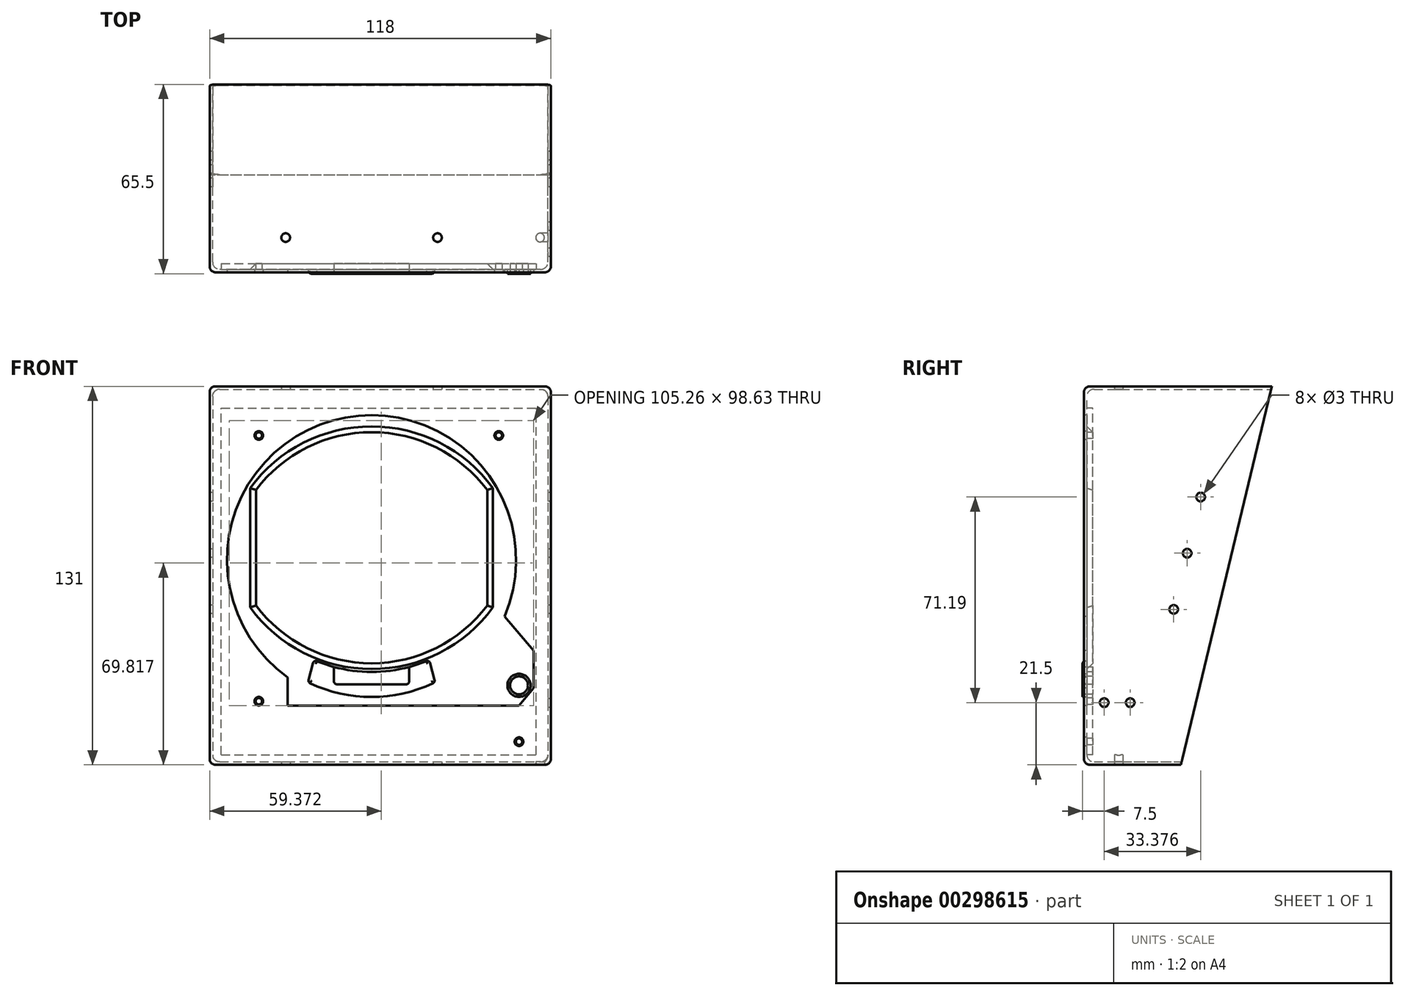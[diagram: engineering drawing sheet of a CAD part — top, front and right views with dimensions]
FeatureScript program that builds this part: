
annotation { "Feature Type Name" : "Feature", "Feature Type Description" : "" }
export const myFeature = defineFeature(function(context is Context, id is Id, definition is map)
    precondition{}
    {
        {
            var Q0;
            Q0=qCreatedBy(makeId("Front.planeOp"),FACE);
            var sketch = newSketch(context, id + "F0", { "sketchPlane" : qUnion([Q0])});
            skLineSegment(sketch, "E0.bottom", {"start": v(-52.84, -65.5) * mm, "end": v(-170.84, -65.5) * mm});
            skLineSegment(sketch, "E0.top", {"start": v(-52.84, 65.5) * mm, "end": v(-170.84, 65.5) * mm});
            skLineSegment(sketch, "E0.left", {"start": v(-52.84, -65.5) * mm, "end": v(-52.84, 65.5) * mm});
            skLineSegment(sketch, "E0.right", {"start": v(-170.84, -65.5) * mm, "end": v(-170.84, 65.5) * mm});
            skPoint(sketch, "E0.middle", {"position": v(-111.84, 0) * mm});
            skSolve(sketch);
        }
        {
            var Q0;
            Q0=makeQuery(id+"F0.imprint","IMPRINT",FACE,{"disambiguationData":[TD([[makeQuery(id+"F0.imprint","IMPRINT",EDGE,{"derivedFrom":sQuery(id+"F0.wireOp",EDGE,"E0.bottom")}),-1.0]])]});
            extrude(context, id + "F1", {"entities" : qUnion([Q0]), "endBound" : BoundingType.SYMMETRIC, "depth" : 120 * mm});
        }
        {
            var Q0;
            Q0=makeQuery(id+"F1.opExtrude","CAP_FACE",FACE,{"disambiguationData":[OSD([sQuery(id+"F0.wireOp",EDGE,"E0.bottom"),sQuery(id+"F0.wireOp",EDGE,"E0.top"),sQuery(id+"F0.wireOp",EDGE,"E0.left"),sQuery(id+"F0.wireOp",EDGE,"E0.right")])],"isStart":true});
            shell(context, id + "F2", {"entities" : qUnion([Q0]), "thickness" : 1 * mm});
        }
        {
            var Q0;
            Q0=makeQuery(id+"F1.opExtrude","SWEPT_FACE",FACE,{"disambiguationData":[OSD([sQuery(id+"F0.wireOp",EDGE,"E0.right")])]});
            var sketch = newSketch(context, id + "F3", { "sketchPlane" : qUnion([Q0])});
            skLineSegment(sketch, "E1", {"start": v(-5, 65.5) * mm, "end": v(26.45, -65.5) * mm});
            skLineSegment(sketch, "E2", {"start": v(26.45, -65.5) * mm, "end": v(-89.83, -65.5) * mm});
            skLineSegment(sketch, "E3", {"start": v(-89.83, -65.5) * mm, "end": v(-89.83, 65.5) * mm});
            skLineSegment(sketch, "E4", {"start": v(-89.83, 65.5) * mm, "end": v(-5, 65.5) * mm});
            skCircle(sketch, "E5", {"center": v(19.62, 27.19) * mm, "radius": 1.5 * mm});
            skCircle(sketch, "E6", {"center": v(28.96, -11.7) * mm, "radius": 1.5 * mm});
            skLineSegment(sketch, "E7", {"start": v(9.7, 4.24) * mm, "end": v(48.51, 13.56) * mm, "construction": true});
            skLineSegment(sketch, "E8", {"start": v(4.8, 24.66) * mm, "end": v(14.6, -16.18) * mm, "construction": true});
            skLineSegment(sketch, "E9", {"start": v(14.6, -16.18) * mm, "end": v(16.55, -15.71) * mm, "construction": true});
            skLineSegment(sketch, "E10", {"start": v(16.55, -15.71) * mm, "end": v(6.75, 25.13) * mm, "construction": true});
            skLineSegment(sketch, "E11", {"start": v(6.75, 25.13) * mm, "end": v(4.8, 24.66) * mm, "construction": true});
            skCircle(sketch, "E12", {"center": v(24.3, 7.74) * mm, "radius": 1.5 * mm});
            skSolve(sketch);
        }
        {
            var Q0;
            Q0=qSketchRegion(id+"F3",true);
            extrude(context, id + "F4", {"entities" : qUnion([Q0]), "operationType" : NewBodyOperationType.REMOVE, "oppositeDirection" : true, "depth" : 150 * mm});
        }
        {
            var Q0;
            Q0=makeQuery(id+"F1.opExtrude","CAP_EDGE",EDGE,{"disambiguationData":[OSD([sQuery(id+"F0.wireOp",EDGE,"E0.right")])],"isStart":false});
            var Q1;
            Q1=makeQuery(id+"F1.opExtrude","SWEPT_EDGE",EDGE,{"disambiguationData":[OSD([sQuery(id+"F0.wireOp",EDGE,"E0.top"),sQuery(id+"F0.wireOp",EDGE,"E0.right")])]});
            var Q2;
            Q2=makeQuery(id+"F1.opExtrude","CAP_EDGE",EDGE,{"disambiguationData":[OSD([sQuery(id+"F0.wireOp",EDGE,"E0.top")])],"isStart":false});
            var Q3;
            Q3=makeQuery(id+"F1.opExtrude","CAP_EDGE",EDGE,{"disambiguationData":[OSD([sQuery(id+"F0.wireOp",EDGE,"E0.left")])],"isStart":false});
            var Q4;
            Q4=makeQuery(id+"F1.opExtrude","SWEPT_EDGE",EDGE,{"disambiguationData":[OSD([sQuery(id+"F0.wireOp",EDGE,"E0.top"),sQuery(id+"F0.wireOp",EDGE,"E0.left")])]});
            var Q5;
            Q5=makeQuery(id+"F1.opExtrude","CAP_EDGE",EDGE,{"disambiguationData":[OSD([sQuery(id+"F0.wireOp",EDGE,"E0.bottom")])],"isStart":false});
            var Q6;
            Q6=makeQuery(id+"F1.opExtrude","SWEPT_EDGE",EDGE,{"disambiguationData":[OSD([sQuery(id+"F0.wireOp",EDGE,"E0.bottom"),sQuery(id+"F0.wireOp",EDGE,"E0.left")])]});
            var Q7;
            Q7=makeQuery(id+"F1.opExtrude","SWEPT_EDGE",EDGE,{"disambiguationData":[OSD([sQuery(id+"F0.wireOp",EDGE,"E0.bottom"),sQuery(id+"F0.wireOp",EDGE,"E0.right")])]});
            fillet(context, id + "F5", {"entities" : qUnion([Q0, Q1, Q2, Q3, Q4, Q5, Q6, Q7]), "radius" : 2 * mm, "tangentPropagation" : true, "allowEdgeOverflow" : false});
        }
        {
            var Q0;
            Q0=makeQuery(id+"F1.opExtrude","CAP_FACE",FACE,{"disambiguationData":[OSD([sQuery(id+"F0.wireOp",EDGE,"E0.bottom"),sQuery(id+"F0.wireOp",EDGE,"E0.top"),sQuery(id+"F0.wireOp",EDGE,"E0.left"),sQuery(id+"F0.wireOp",EDGE,"E0.right")])],"isStart":false});
            var sketch = newSketch(context, id + "F6", { "sketchPlane" : qUnion([Q0])});
            skCircle(sketch, "E13", {"center": v(-114.84, 5.5) * mm, "radius": 50 * mm});
            skLineSegment(sketch, "E14", {"start": v(-143.84, -35.23) * mm, "end": v(-143.84, -45) * mm});
            skLineSegment(sketch, "E15", {"start": v(-143.84, -45) * mm, "end": v(-63.84, -45) * mm});
            skLineSegment(sketch, "E16", {"start": v(-63.84, -45) * mm, "end": v(-58.84, -39) * mm});
            skLineSegment(sketch, "E17", {"start": v(-58.84, -39) * mm, "end": v(-58.84, -26) * mm});
            skLineSegment(sketch, "E18", {"start": v(-58.84, -26) * mm, "end": v(-68.86, -14.15) * mm});
            skCircle(sketch, "E19", {"center": v(-153.84, 48.5) * mm, "radius": 1.5 * mm});
            skCircle(sketch, "E20", {"center": v(-70.84, 48.5) * mm, "radius": 1.5 * mm});
            skCircle(sketch, "E21", {"center": v(-153.84, -43.5) * mm, "radius": 1.5 * mm});
            skCircle(sketch, "E22", {"center": v(-63.84, -57.5) * mm, "radius": 1.5 * mm});
            skSolve(sketch);
        }
        {
            var Q0;
            Q0=qSketchRegion(id+"F6",true);
            extrude(context, id + "F7", {"entities" : qUnion([Q0]), "operationType" : NewBodyOperationType.REMOVE, "oppositeDirection" : true, "depth" : 1 * mm});
        }
        {
            var Q0;
            Q0=makeQuery(id+"F2.opShell","OFFSET_FACE",FACE,{"disambiguationData":[OSD([sQuery(id+"F0.wireOp",EDGE,"E0.bottom"),sQuery(id+"F0.wireOp",EDGE,"E0.top"),sQuery(id+"F0.wireOp",EDGE,"E0.left"),sQuery(id+"F0.wireOp",EDGE,"E0.right")])]});
            var sketch = newSketch(context, id + "F8", { "sketchPlane" : qUnion([Q0])});
            skLineSegment(sketch, "E23.bottom", {"start": v(166.84, -62) * mm, "end": v(57.84, -62) * mm});
            skLineSegment(sketch, "E23.top", {"start": v(166.84, 58) * mm, "end": v(57.84, 58) * mm});
            skLineSegment(sketch, "E23.left", {"start": v(166.84, -62) * mm, "end": v(166.84, 58) * mm});
            skLineSegment(sketch, "E23.right", {"start": v(57.84, -62) * mm, "end": v(57.84, 58) * mm});
            skPoint(sketch, "E23.middle", {"position": v(114.84, 5.5) * mm});
            skCircle(sketch, "E24", {"center": v(153.84, 48.5) * mm, "radius": 1.1 * mm});
            skCircle(sketch, "E25", {"center": v(70.84, 48.5) * mm, "radius": 1.1 * mm});
            skCircle(sketch, "E26", {"center": v(63.84, -57.5) * mm, "radius": 1.1 * mm});
            skCircle(sketch, "E27", {"center": v(153.84, -43.5) * mm, "radius": 1.1 * mm});
            skCircle(sketch, "E28", {"center": v(63.84, -38) * mm, "radius": 3.1 * mm});
            skLineSegment(sketch, "E29.bottom", {"start": v(74.84, -10.37) * mm, "end": v(154.84, -10.37) * mm, "construction": true});
            skLineSegment(sketch, "E29.top", {"start": v(74.84, 29.63) * mm, "end": v(154.84, 29.63) * mm, "construction": true});
            skLineSegment(sketch, "E29.left", {"start": v(74.84, -10.37) * mm, "end": v(74.84, 29.63) * mm});
            skLineSegment(sketch, "E29.right", {"start": v(154.84, -10.37) * mm, "end": v(154.84, 29.63) * mm});
            skPoint(sketch, "E29.middle", {"position": v(114.84, 9.63) * mm});
            skArc(sketch, "E30", {"start": v(154.84, 29.63) * mm, "mid": v(114.84, 49.63) * mm, "end": v(74.84, 29.63) * mm});
            skArc(sketch, "E31", {"start": v(74.84, -10.37) * mm, "mid": v(114.84, -30.37) * mm, "end": v(154.84, -10.37) * mm});
            skSolve(sketch);
        }
        {
            var Q0;
            Q0=qSketchRegion(id+"F8",true);
            extrude(context, id + "F9", {"entities" : qUnion([Q0]), "depth" : 2 * mm});
        }
        {
            var Q0;
            Q0=makeQuery(id+"F9.opExtrude","CAP_FACE",FACE,{"disambiguationData":[OSD([sQuery(id+"F8.wireOp",EDGE,"E23.bottom"),sQuery(id+"F8.wireOp",EDGE,"E23.top"),sQuery(id+"F8.wireOp",EDGE,"E23.left"),sQuery(id+"F8.wireOp",EDGE,"E23.right"),sQuery(id+"F8.wireOp",EDGE,"E24"),sQuery(id+"F8.wireOp",EDGE,"E25"),sQuery(id+"F8.wireOp",EDGE,"E26"),sQuery(id+"F8.wireOp",EDGE,"E27"),sQuery(id+"F8.wireOp",EDGE,"E28"),sQuery(id+"F8.wireOp",EDGE,"E29.left"),sQuery(id+"F8.wireOp",EDGE,"E29.right"),sQuery(id+"F8.wireOp",EDGE,"E30"),sQuery(id+"F8.wireOp",EDGE,"E31")])],"isStart":true});
            var sketch = newSketch(context, id + "F10", { "sketchPlane" : qUnion([Q0])});
            skArc(sketch, "E32", {"start": v(-134.84, -29.2) * mm, "mid": v(-114.84, -33.37) * mm, "end": v(-94.84, -29.2) * mm});
            skPoint(sketch, "E33", {"position": v(-114.84, -30.37) * mm});
            skArc(sketch, "E34", {"start": v(-136.84, -36.94) * mm, "mid": v(-114.84, -42.04) * mm, "end": v(-92.84, -36.94) * mm});
            skLineSegment(sketch, "E35", {"start": v(-134.84, -29.2) * mm, "end": v(-136.84, -36.94) * mm});
            skLineSegment(sketch, "E36", {"start": v(-94.84, -29.2) * mm, "end": v(-92.84, -36.94) * mm});
            skCircle(sketch, "E37", {"center": v(-63.84, -38) * mm, "radius": 4 * mm});
            skCircle(sketch, "E38", {"center": v(-63.84, -38) * mm, "radius": 3.1 * mm});
            skSolve(sketch);
        }
        {
            var Q0;
            Q0 = qSketchRegion(id + "F10", true);
            extrude(context, id + "F11", {"entities" : qUnion([Q0]), "operationType" : NewBodyOperationType.ADD, "depth" : 1.5 * mm});
        }
        {
            var Q0;
            Q0=makeQuery(id+"F11.opExtrude","CAP_FACE",FACE,{"disambiguationData":[OSD([sQuery(id+"F10.wireOp",EDGE,"E32"),sQuery(id+"F10.wireOp",EDGE,"E34"),sQuery(id+"F10.wireOp",EDGE,"E35"),sQuery(id+"F10.wireOp",EDGE,"E36")])],"isStart":false});
            var sketch = newSketch(context, id + "F12", { "sketchPlane" : qUnion([Q0])});
            skLineSegment(sketch, "E39", {"start": v(-127.84, -31.65) * mm, "end": v(-127.84, -37.65) * mm});
            skLineSegment(sketch, "E40", {"start": v(-127.84, -37.65) * mm, "end": v(-101.84, -37.65) * mm});
            skLineSegment(sketch, "E41", {"start": v(-101.84, -37.65) * mm, "end": v(-101.84, -31.65) * mm});
            skArc(sketch, "E42", {"start": v(-127.84, -31.65) * mm, "mid": v(-114.84, -33.37) * mm, "end": v(-101.84, -31.65) * mm});
            skSolve(sketch);
        }
        {
            var Q0;
            Q0 = qSketchRegion(id + "F12", true);
            extrude(context, id + "F13", {"entities" : qUnion([Q0]), "operationType" : NewBodyOperationType.REMOVE, "oppositeDirection" : true, "depth" : 25 * mm});
        }
        {
            var Q0;
            Q0=makeQuery(id+"F11.opExtrude","CAP_EDGE",EDGE,{"disambiguationData":[OSD([sQuery(id+"F10.wireOp",EDGE,"E35")])],"isStart":false});
            var Q1;
            Q1=makeQuery(id+"F11.opExtrude","CAP_EDGE",EDGE,{"disambiguationData":[OSD([sQuery(id+"F10.wireOp",EDGE,"E34")])],"isStart":false});
            var Q2;
            {var subQ0=sQuery(id+"F10.wireOp",EDGE,"E32");var subQ1=sQuery(id+"F10.wireOp",EDGE,"E35");Q2=makeQuery(id+"F13.boolean.opBoolean","SPLIT",EDGE,{"disambiguationData":[TD([makeQuery(id+"F11.opExtrude","SWEPT_FACE",FACE,{"disambiguationData":[OSD([subQ1])]})])],"derivedFrom":makeQuery(id+"F11.opExtrude","CAP_EDGE",EDGE,{"disambiguationData":[OSD([subQ0])],"isStart":false})});}
            var Q3;
            Q3=makeQuery(id+"F11.opExtrude","CAP_EDGE",EDGE,{"disambiguationData":[OSD([sQuery(id+"F10.wireOp",EDGE,"E36")])],"isStart":false});
            var Q4;
            {var subQ0=sQuery(id+"F10.wireOp",EDGE,"E32");var subQ1=sQuery(id+"F10.wireOp",EDGE,"E36");Q4=makeQuery(id+"F13.boolean.opBoolean","SPLIT",EDGE,{"disambiguationData":[TD([makeQuery(id+"F11.opExtrude","SWEPT_FACE",FACE,{"disambiguationData":[OSD([subQ1])]})])],"derivedFrom":makeQuery(id+"F11.opExtrude","CAP_EDGE",EDGE,{"disambiguationData":[OSD([subQ0])],"isStart":false})});}
            fillet(context, id + "F14", {"entities" : qUnion([Q0, Q1, Q2, Q3, Q4]), "radius" : 1 * mm, "tangentPropagation" : true, "allowEdgeOverflow" : false});
        }
        {
            var Q0;
            Q0=makeQuery(id+"F14.opFillet","BLEND_EDGE",EDGE,{"blendedFrom":[makeQuery(id+"F11.opExtrude","CAP_EDGE",EDGE,{"disambiguationData":[OSD([sQuery(id+"F10.wireOp",EDGE,"E34")])],"isStart":false}),makeQuery(id+"F11.opExtrude","CAP_EDGE",EDGE,{"disambiguationData":[OSD([sQuery(id+"F10.wireOp",EDGE,"E35")])],"isStart":false})],"blendedInto":[]});
            var Q1;
            {var subQ0=sQuery(id+"F10.wireOp",EDGE,"E32");var subQ1=sQuery(id+"F10.wireOp",EDGE,"E35");Q1=makeQuery(id+"F14.opFillet","BLEND_EDGE",EDGE,{"blendedFrom":[makeQuery(id+"F11.opExtrude","CAP_EDGE",EDGE,{"disambiguationData":[OSD([subQ1])],"isStart":false}),makeQuery(id+"F13.boolean.opBoolean","SPLIT",EDGE,{"disambiguationData":[TD([makeQuery(id+"F11.opExtrude","SWEPT_FACE",FACE,{"disambiguationData":[OSD([subQ1])]})])],"derivedFrom":makeQuery(id+"F11.opExtrude","CAP_EDGE",EDGE,{"disambiguationData":[OSD([subQ0])],"isStart":false})})],"blendedInto":[]});}
            var Q2;
            {var subQ0=sQuery(id+"F10.wireOp",EDGE,"E32");var subQ1=sQuery(id+"F10.wireOp",EDGE,"E36");Q2=makeQuery(id+"F14.opFillet","BLEND_EDGE",EDGE,{"blendedFrom":[makeQuery(id+"F11.opExtrude","CAP_EDGE",EDGE,{"disambiguationData":[OSD([subQ1])],"isStart":false}),makeQuery(id+"F13.boolean.opBoolean","SPLIT",EDGE,{"disambiguationData":[TD([makeQuery(id+"F11.opExtrude","SWEPT_FACE",FACE,{"disambiguationData":[OSD([subQ1])]})])],"derivedFrom":makeQuery(id+"F11.opExtrude","CAP_EDGE",EDGE,{"disambiguationData":[OSD([subQ0])],"isStart":false})})],"blendedInto":[]});}
            var Q3;
            Q3=makeQuery(id+"F14.opFillet","BLEND_EDGE",EDGE,{"blendedFrom":[makeQuery(id+"F11.opExtrude","CAP_EDGE",EDGE,{"disambiguationData":[OSD([sQuery(id+"F10.wireOp",EDGE,"E34")])],"isStart":false}),makeQuery(id+"F11.opExtrude","CAP_EDGE",EDGE,{"disambiguationData":[OSD([sQuery(id+"F10.wireOp",EDGE,"E36")])],"isStart":false})],"blendedInto":[]});
            var Q4;
            Q4=makeQuery(id+"F13.boolean.opBoolean","COPY",EDGE,{"derivedFrom":makeQuery(id+"F13.opExtrude","SWEPT_EDGE",EDGE,{"disambiguationData":[OSD([sQuery(id+"F12.wireOp",EDGE,"E39"),sQuery(id+"F12.wireOp",EDGE,"E40")])]})});
            var Q5;
            Q5=makeQuery(id+"F13.boolean.opBoolean","COPY",EDGE,{"derivedFrom":makeQuery(id+"F13.opExtrude","SWEPT_EDGE",EDGE,{"disambiguationData":[OSD([sQuery(id+"F12.wireOp",EDGE,"E40"),sQuery(id+"F12.wireOp",EDGE,"E41")])]})});
            fillet(context, id + "F15", {"entities" : qUnion([Q0, Q1, Q2, Q3, Q4, Q5]), "radius" : 1 * mm, "tangentPropagation" : true, "allowEdgeOverflow" : false});
        }
        {
            var Q0;
            Q0=makeQuery(id+"F9.opExtrude","CAP_EDGE",EDGE,{"disambiguationData":[OSD([sQuery(id+"F8.wireOp",EDGE,"E29.right")])],"isStart":true});
            var Q1;
            Q1=makeQuery(id+"F9.opExtrude","CAP_EDGE",EDGE,{"disambiguationData":[OSD([sQuery(id+"F8.wireOp",EDGE,"E30")])],"isStart":true});
            var Q2;
            Q2=makeQuery(id+"F9.opExtrude","CAP_EDGE",EDGE,{"disambiguationData":[OSD([sQuery(id+"F8.wireOp",EDGE,"E29.left")])],"isStart":true});
            var Q3;
            Q3=makeQuery(id+"F9.opExtrude","CAP_EDGE",EDGE,{"disambiguationData":[OSD([sQuery(id+"F8.wireOp",EDGE,"E31")])],"isStart":true});
            chamfer(context, id + "F16", {"entities" : qUnion([Q0, Q1, Q2, Q3]), "width" : 2 * mm, "tangentPropagation" : true});
        }
        {
            var Q0;
            Q0=makeQuery(id+"F1.opExtrude","SWEPT_FACE",FACE,{"disambiguationData":[OSD([sQuery(id+"F0.wireOp",EDGE,"E0.bottom")])]});
            var sketch = newSketch(context, id + "F17", { "sketchPlane" : qUnion([Q0])});
            skCircle(sketch, "E43", {"center": v(-144.54, 48) * mm, "radius": 1.5 * mm});
            skCircle(sketch, "E44", {"center": v(-92.04, 48) * mm, "radius": 1.5 * mm});
            skCircle(sketch, "E45", {"center": v(-56.54, 48) * mm, "radius": 1.5 * mm, "construction": true});
            skSolve(sketch);
        }
        {
            var Q0;
            Q0 = qSketchRegion(id + "F17", true);
            extrude(context, id + "F18", {"entities" : qUnion([Q0]), "operationType" : NewBodyOperationType.REMOVE, "endBound" : BoundingType.THROUGH_ALL, "oppositeDirection" : true, "depth" : 25 * mm});
        }
        {
            var Q0;
            Q0=makeQuery(id+"F1.opExtrude","SWEPT_FACE",FACE,{"disambiguationData":[OSD([sQuery(id+"F0.wireOp",EDGE,"E0.left")])]});
            var sketch = newSketch(context, id + "F19", { "sketchPlane" : qUnion([Q0])});
            skCircle(sketch, "E46", {"center": v(-53, -44) * mm, "radius": 1.5 * mm});
            skCircle(sketch, "E47", {"center": v(-44, -44) * mm, "radius": 1.5 * mm});
            skSolve(sketch);
        }
        {
            var Q0;
            Q0 = qSketchRegion(id + "F19", true);
            extrude(context, id + "F20", {"entities" : qUnion([Q0]), "operationType" : NewBodyOperationType.REMOVE, "oppositeDirection" : true, "depth" : 2 * mm});
        }
        {
            var Q0;
            Q0=makeQuery(id+"F1.opExtrude","SWEPT_FACE",FACE,{"disambiguationData":[OSD([sQuery(id+"F0.wireOp",EDGE,"E0.bottom")])]});
            var sketch = newSketch(context, id + "F21", { "sketchPlane" : qUnion([Q0])});
            skCircle(sketch, "E48", {"center": v(-56.54, 48) * mm, "radius": 1.5 * mm});
            skSolve(sketch);
        }
        {
            var Q0;
            Q0 = qSketchRegion(id + "F21", true);
            extrude(context, id + "F22", {"entities" : qUnion([Q0]), "operationType" : NewBodyOperationType.REMOVE, "oppositeDirection" : true, "depth" : 2 * mm});
        }
        {
            var Q0;
            {var subQ0=sQuery(id+"F0.wireOp",EDGE,"E0.left");Q0=makeQuery(id+"F2.opShell","OFFSET_EDGE",EDGE,{"disambiguationData":[OSD([subQ0]),TDD([makeQuery(id+"F1.opExtrude","CAP_EDGE",EDGE,{"disambiguationData":[OSD([subQ0])],"isStart":false})])]});}
            var Q1;
            {var subQ0=sQuery(id+"F0.wireOp",EDGE,"E0.top");Q1=makeQuery(id+"F2.opShell","OFFSET_EDGE",EDGE,{"disambiguationData":[OSD([subQ0]),TDD([makeQuery(id+"F1.opExtrude","CAP_EDGE",EDGE,{"disambiguationData":[OSD([subQ0])],"isStart":false})])]});}
            var Q2;
            {var subQ0=sQuery(id+"F0.wireOp",EDGE,"E0.right");Q2=makeQuery(id+"F2.opShell","OFFSET_EDGE",EDGE,{"disambiguationData":[OSD([subQ0]),TDD([makeQuery(id+"F1.opExtrude","CAP_EDGE",EDGE,{"disambiguationData":[OSD([subQ0])],"isStart":false})])]});}
            var Q3;
            {var subQ0=sQuery(id+"F0.wireOp",EDGE,"E0.bottom");Q3=makeQuery(id+"F2.opShell","OFFSET_EDGE",EDGE,{"disambiguationData":[OSD([subQ0]),TDD([makeQuery(id+"F1.opExtrude","CAP_EDGE",EDGE,{"disambiguationData":[OSD([subQ0])],"isStart":false})])]});}
            var Q4;
            Q4=makeQuery(id+"F2.opShell","OFFSET_EDGE",EDGE,{"disambiguationData":[OSD([sQuery(id+"F0.wireOp",EDGE,"E0.bottom"),sQuery(id+"F0.wireOp",EDGE,"E0.right")])]});
            var Q5;
            Q5=makeQuery(id+"F2.opShell","OFFSET_EDGE",EDGE,{"disambiguationData":[OSD([sQuery(id+"F0.wireOp",EDGE,"E0.bottom"),sQuery(id+"F0.wireOp",EDGE,"E0.left")])]});
            var Q6;
            Q6=makeQuery(id+"F2.opShell","OFFSET_EDGE",EDGE,{"disambiguationData":[OSD([sQuery(id+"F0.wireOp",EDGE,"E0.top"),sQuery(id+"F0.wireOp",EDGE,"E0.left")])]});
            var Q7;
            Q7=makeQuery(id+"F2.opShell","OFFSET_EDGE",EDGE,{"disambiguationData":[OSD([sQuery(id+"F0.wireOp",EDGE,"E0.top"),sQuery(id+"F0.wireOp",EDGE,"E0.right")])]});
            fillet(context, id + "F23", {"entities" : qUnion([Q0, Q1, Q2, Q3, Q4, Q5, Q6, Q7]), "radius" : 2.5 * mm, "tangentPropagation" : true, "allowEdgeOverflow" : false});
        }
    });
